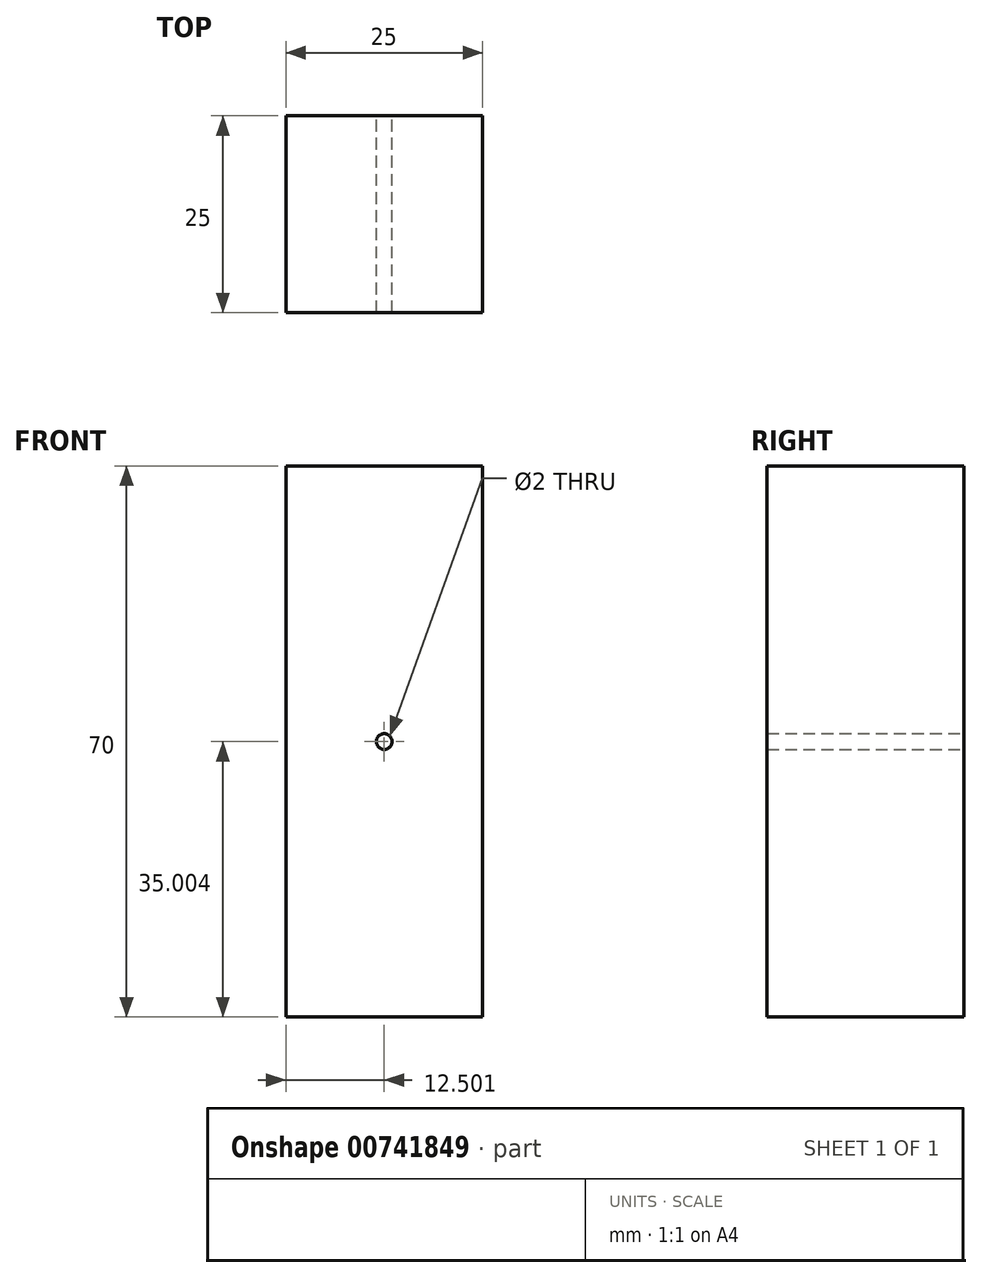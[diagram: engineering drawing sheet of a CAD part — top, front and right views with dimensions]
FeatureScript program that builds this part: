
annotation { "Feature Type Name" : "Feature", "Feature Type Description" : "" }
export const myFeature = defineFeature(function(context is Context, id is Id, definition is map)
    precondition{}
    {
        {
            var Q0;
            Q0=qCreatedBy(makeId("Front.planeOp"),FACE);
            var sketch = newSketch(context, id + "F0", { "sketchPlane" : qUnion([Q0])});
            skLineSegment(sketch, "E0.bottom", {"start": v(-21.42, 51.4) * mm, "end": v(3.58, 51.4) * mm});
            skLineSegment(sketch, "E0.top", {"start": v(-21.42, -18.6) * mm, "end": v(3.58, -18.6) * mm});
            skLineSegment(sketch, "E0.left", {"start": v(-21.42, 51.4) * mm, "end": v(-21.42, -18.6) * mm});
            skLineSegment(sketch, "E0.right", {"start": v(3.58, 51.4) * mm, "end": v(3.58, -18.6) * mm});
            skCircle(sketch, "E1", {"center": v(-8.92, 16.4) * mm, "radius": 1 * mm});
            skSolve(sketch);
        }
        {
            var Q0;
            Q0 = qSketchRegion(id + "F0", true);
            extrude(context, id + "F1", {"entities" : qUnion([Q0]), "depth" : 25 * mm, "offsetDistance" : 25 * mm});
        }
    });
